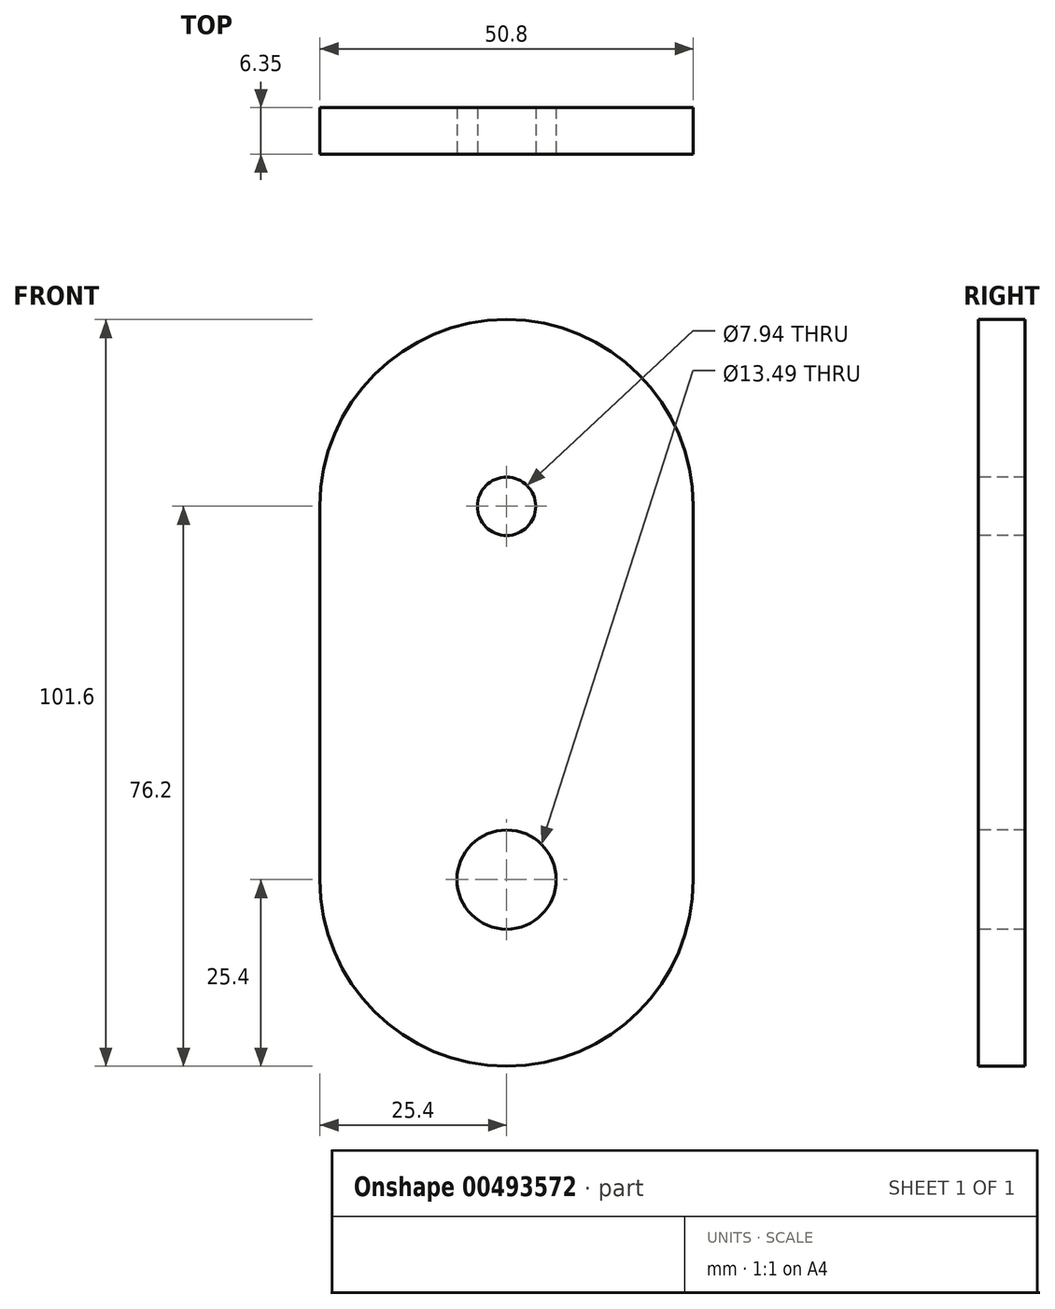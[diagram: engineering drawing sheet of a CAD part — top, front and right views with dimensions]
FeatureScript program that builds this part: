
annotation { "Feature Type Name" : "Feature", "Feature Type Description" : "" }
export const myFeature = defineFeature(function(context is Context, id is Id, definition is map)
    precondition{}
    {
        {
            var Q0;
            Q0=qCreatedBy(makeId("Front.planeOp"),FACE);
            var sketch = newSketch(context, id + "F0", { "sketchPlane" : qUnion([Q0])});
            skArc(sketch, "E0", {"start": v(-25.4, 0) * mm, "mid": v(0, -25.4) * mm, "end": v(25.4, 0) * mm});
            skLineSegment(sketch, "E1", {"start": v(-25.4, 0) * mm, "end": v(-25.4, 50.8) * mm});
            skArc(sketch, "E2", {"start": v(25.4, 50.8) * mm, "mid": v(0, 76.2) * mm, "end": v(-25.4, 50.8) * mm});
            skLineSegment(sketch, "E3", {"start": v(25.4, 50.8) * mm, "end": v(25.4, 0) * mm});
            skSolve(sketch);
        }
        {
            var Q0;
            Q0 = qSketchRegion(id + "F0", true);
            extrude(context, id + "F1", {"entities" : qUnion([Q0]), "depth" : 6.35 * mm});
        }
        {
            var Q0;
            Q0=makeQuery(id+"F1.opExtrude","CAP_FACE",FACE,{"disambiguationData":[OSD([sQuery(id+"F0.wireOp",EDGE,"E0"),sQuery(id+"F0.wireOp",EDGE,"E1"),sQuery(id+"F0.wireOp",EDGE,"E2"),sQuery(id+"F0.wireOp",EDGE,"E3")])],"isStart":false});
            var sketch = newSketch(context, id + "F2", { "sketchPlane" : qUnion([Q0])});
            skPoint(sketch, "E4", {"position": v(0, 0) * mm});
            skPoint(sketch, "E5", {"position": v(0, 50.8) * mm});
            skSolve(sketch);
        }
        {
            var Q0;
            Q0=sQuery(id+"F2.wireOp",VERTEX,"E5");
            var Q1;
            Q1=makeQuery(id+"F1.opExtrude","SWEPT_BODY",BODY,{"disambiguationData":[OSD([sQuery(id+"F0.wireOp",EDGE,"E0"),sQuery(id+"F0.wireOp",EDGE,"E1"),sQuery(id+"F0.wireOp",EDGE,"E2"),sQuery(id+"F0.wireOp",EDGE,"E3")])]});
            hole(context, id + "F3", {"style" : HoleStyle.SIMPLE, "endStyle" : HoleEndStyle.THROUGH, "standardTappedOrClearance" : lookupTablePath({ "standard" : "ANSI", "engagement" : "75%", "pitch" : "16 tpi", "size" : "3/8", "type" : "Tapped" }), "standardBlindInLast" : lookupTablePath({ "standard" : "ANSI", "engagement" : "75%", "pitch" : "16 tpi", "size" : "3/8", "type" : "Tapped" }), "holeDiameter" : 7.94 * mm, "showTappedDepth" : true, "tappedDepth" : 20.65 * mm, "tapClearance" : 3, "startFromSketch" : true, "locations" : qUnion([Q0]), "scope" : qUnion([Q1]), "majorDiameter" : 9.53 * mm});
        }
        {
            var Q0;
            Q0=makeQuery(id+"F1.opExtrude","CAP_FACE",FACE,{"disambiguationData":[OSD([sQuery(id+"F0.wireOp",EDGE,"E0"),sQuery(id+"F0.wireOp",EDGE,"E1"),sQuery(id+"F0.wireOp",EDGE,"E2"),sQuery(id+"F0.wireOp",EDGE,"E3")])],"isStart":false});
            var sketch = newSketch(context, id + "F4", { "sketchPlane" : qUnion([Q0])});
            skPoint(sketch, "E6", {"position": v(0, 0) * mm});
            skSolve(sketch);
        }
        {
            var Q0;
            Q0=sQuery(id+"F4.wireOp",VERTEX,"E6");
            var Q1;
            Q1=makeQuery(id+"F1.opExtrude","SWEPT_BODY",BODY,{"disambiguationData":[OSD([sQuery(id+"F0.wireOp",EDGE,"E0"),sQuery(id+"F0.wireOp",EDGE,"E1"),sQuery(id+"F0.wireOp",EDGE,"E2"),sQuery(id+"F0.wireOp",EDGE,"E3")])]});
            hole(context, id + "F5", {"style" : HoleStyle.SIMPLE, "endStyle" : HoleEndStyle.THROUGH, "standardTappedOrClearance" : lookupTablePath({ "standard" : "ANSI", "fit" : "Normal (ASME)", "size" : "1/2", "type" : "Clearance" }), "standardBlindInLast" : lookupTablePath({ "fit" : "Free", "standard" : "ANSI", "size" : "1/2", "type" : "Clearance" }), "holeDiameter" : 13.5 * mm, "tappedDepth" : 20.65 * mm, "tapClearance" : 3, "startFromSketch" : true, "locations" : qUnion([Q0]), "scope" : qUnion([Q1])});
        }
    });
